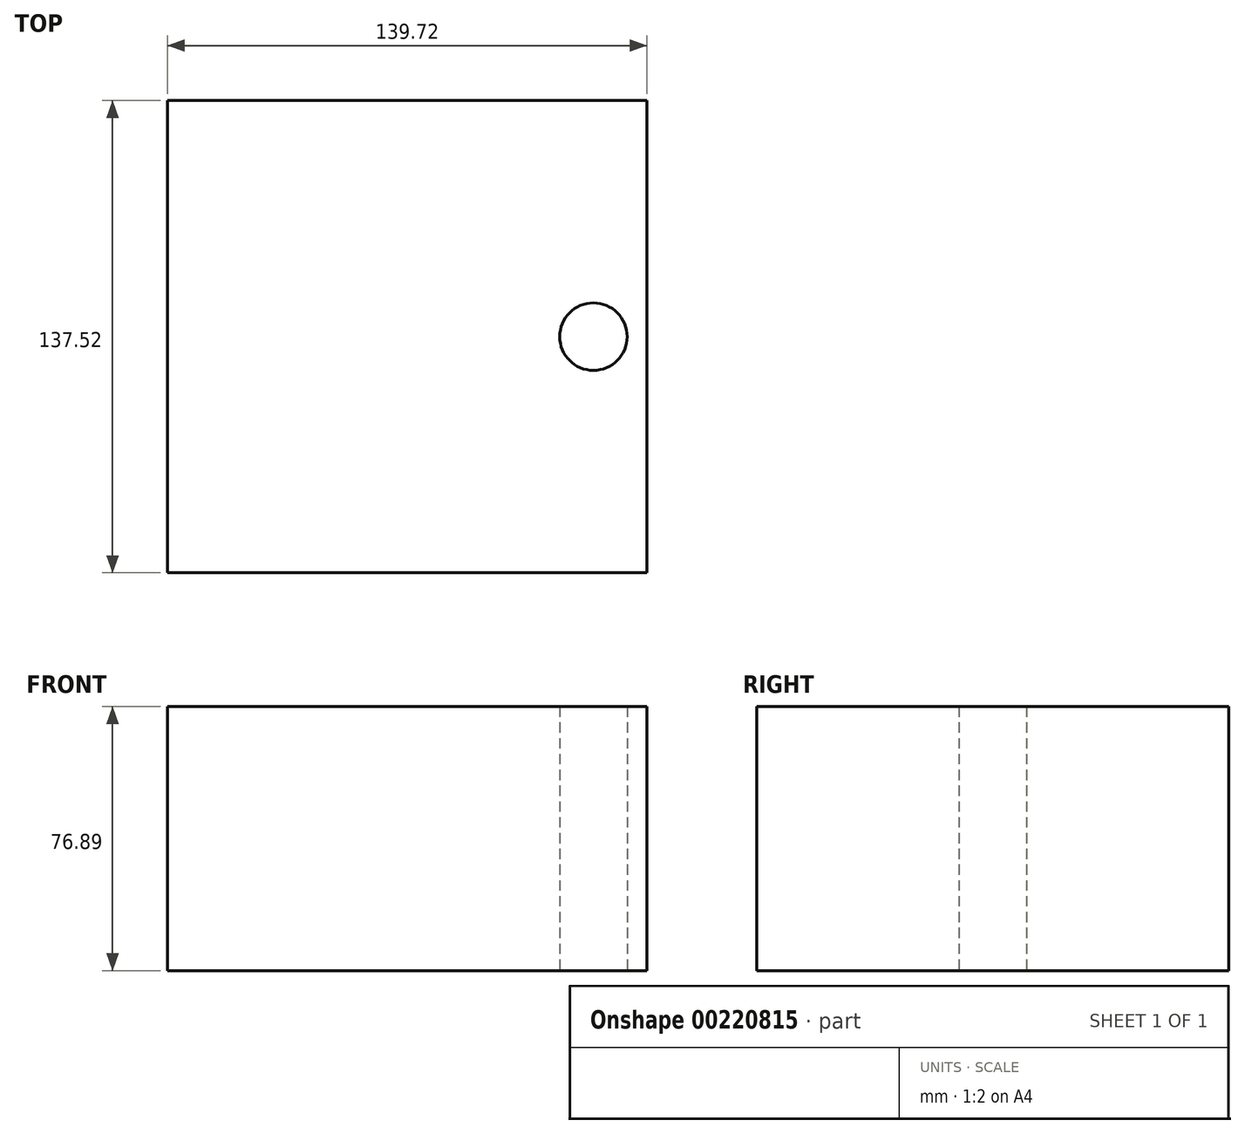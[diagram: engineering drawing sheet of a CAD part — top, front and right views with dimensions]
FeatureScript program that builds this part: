
annotation { "Feature Type Name" : "Feature", "Feature Type Description" : "" }
export const myFeature = defineFeature(function(context is Context, id is Id, definition is map)
    precondition{}
    {
        {
            var Q0;
            Q0=qCreatedBy(makeId("Top.planeOp"),FACE);
            var sketch = newSketch(context, id + "F0", { "sketchPlane" : qUnion([Q0])});
            skLineSegment(sketch, "E0.bottom", {"start": v(69.86, -68.76) * mm, "end": v(-69.86, -68.76) * mm});
            skLineSegment(sketch, "E0.top", {"start": v(69.86, 68.76) * mm, "end": v(-69.86, 68.76) * mm});
            skLineSegment(sketch, "E0.left", {"start": v(69.86, -68.76) * mm, "end": v(69.86, 68.76) * mm});
            skLineSegment(sketch, "E0.right", {"start": v(-69.86, -68.76) * mm, "end": v(-69.86, 68.76) * mm});
            skPoint(sketch, "E0.middle", {"position": v(0, 0) * mm});
            skLineSegment(sketch, "E1", {"start": v(0, 68.76) * mm, "end": v(0, -68.76) * mm});
            skSolve(sketch);
        }
        {
            var Q0;
            Q0=qCreatedBy(makeId("Top.planeOp"),FACE);
            var sketch = newSketch(context, id + "F1", { "sketchPlane" : qUnion([Q0])});
            skCircle(sketch, "E2", {"center": v(54.26, 0) * mm, "radius": 9.82 * mm});
            skSolve(sketch);
        }
        {
            var Q0;
            {var subQ0=sQuery(id+"F0.wireOp",EDGE,"E0.left");Q0=makeQuery(id+"F0.imprint","IMPRINT",FACE,{"disambiguationData":[TD([[makeQuery(id+"F0.imprint","IMPRINT",EDGE,{"derivedFrom":subQ0}),1.0]])]});}
            var Q1;
            {var subQ0=sQuery(id+"F0.wireOp",EDGE,"E0.right");Q1=makeQuery(id+"F0.imprint","IMPRINT",FACE,{"disambiguationData":[TD([[makeQuery(id+"F0.imprint","IMPRINT",EDGE,{"derivedFrom":subQ0}),-1.0]])]});}
            var Q2;
            Q2=makeQuery(id+"F1.imprint","IMPRINT",FACE,{"disambiguationData":[TD([[makeQuery(id+"F1.imprint","IMPRINT",EDGE,{"derivedFrom":sQuery(id+"F1.wireOp",EDGE,"E2")}),1.0]])]});
            extrude(context, id + "F2", {"entities" : qUnion([Q0, Q1, Q2]), "depth" : 76.89 * mm});
        }
        {
            var Q0;
            Q0=makeQuery(id+"F2.opExtrude","CAP_EDGE",EDGE,{"disambiguationData":[OSD([sQuery(id+"F1.wireOp",EDGE,"E2")])],"isStart":true});
            var Q1;
            Q1=sQuery(id+"F0.wireOp",EDGE,"E1");
            revolve(context, id + "F3", {"bodyType" : ToolBodyType.SURFACE, "surfaceEntities" : qUnion([Q0]), "axis" : qUnion([Q1]), "revolveType" : RevolveType.FULL});
        }
    });
